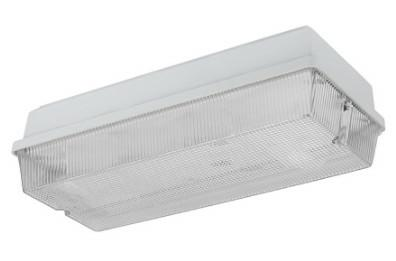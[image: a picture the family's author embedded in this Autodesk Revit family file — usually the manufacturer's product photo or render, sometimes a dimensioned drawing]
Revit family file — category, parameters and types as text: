
# Revit family: GALAD Аларм LED
name_source: partatom
category: Осветительные приборы
revit_build: Autodesk Revit 2018 (Build: 20180423_1000(x64)
units: mm (PartAtom-declared; Revit-internal decimal feet)

## family parameters
Источник света = Да
Общий = Нет
Основа = Грань
При загрузке вырезать с полостями = Нет
Размер круглого соединителя = Использовать диаметр
Тип детали = Нормальный
Точка расчета площади = Нет

## types (1)
- GALAD Аларм LED
    ADSK_Версия Revit = 2018
    ADSK_Версия семейства = 1.01
    ADSK_Единица измерения = шт.
    ADSK_Завод-изготовитель = АО «КАДОШКИНСКИЙ ЭЛЕКТРОТЕХНИЧЕСКИЙ ЗАВОД»
    ADSK_Классификация нагрузок = Освещение
    ADSK_Код изделия = 13653
    ADSK_Количество = 1
    ADSK_Количество фаз = 1
    ADSK_Коэффициент мощности = 0.95
    ADSK_Марка = GALAD Аларм LED-24 4000К БАП
    ADSK_Масса = 2
    ADSK_Масса_Текст = 2.00
    ADSK_Наименование = GALAD Аларм LED-24 4000К БАП
    ADSK_Наименование краткое = GALAD Аларм LED-24 4000К БАП
    ADSK_Напряжение = 230 В
    ADSK_Номинальная мощность = 12 В·А
    ADSK_Обозначение = ГОСТ 15150-69
    ADSK_Полная мощность = 13 В·А
    ADSK_Размер_Высота = 107 мм
    ADSK_Размер_Длина = 376 мм
    ADSK_Размер_Ширина = 156 мм
    ADSK_Ток = 0 А
    ADSK_Энергоэффективность = 79 лм/Вт
    IP = 65
    URL = https://galad.ru
    Блок аварийного питания = Да
    Борт = 6 мм
    Верхняя подсечка = 16 мм
    Видимая форма излучения при визуализации = Нет
    Возможный угол наклона = 0
    Группа модели = Светильники
    Диапазон цветовой температуры = 3985±275
    Излучение по длине прямоугольника = 344 мм
    Излучение по ширине прямоугольника = 124 мм
    Класс Защиты = 1
    Класс защиты от поражения электрическим током = 1
    Класс светораспределения = П
    Климатическая зона = УХЛ4
    Климатическое исполнение = 1…35 °С
    Комментарии к типоразмеру = АО «КАДОШКИНСКИЙ ЭЛЕКТРОТЕХНИЧЕСКИЙ ЗАВОД»
    Коэффициент пульсации = менее 5%
    Материал корпуса = ПММА
    Материал рассеивателя = Поликарбонат
    Неравномерность яркости = 0
    Нижняя подсечка = 25 мм
    Область использования = ЖКХ
    Описание = Светодиодный светильник GALAD Аларм LED - это универсальное решение задачи, изготавливается в аварийном исполнении и в исполнении для использования в качестве светильника основного света
    Отметка по умолчанию = 1219 мм
    Полная установленная мощность = 13 В·А
    Световая отдача = 79
    Светофильтр = 16777215
    Смещение цветовой температуры при затухании лампы = <Нет>
    Снижение светового потока во время разгорания = не более 6%
    Срок службы = 12 лет
    Тип КСС = косинусная
    Тип ПРА = ЭПРА
    Тип источника света = LED
    Тип монтажной поверхности = настенный
    Тип продукции = Светильник
    Тип устройства управления светодиодами = без управления
    Угол наклона = 90.00°
    Файл фотометрической сетки = GALAD alarm LED-24 4000k bap.IES
    Цветопередача = 80
    Частота = 50
